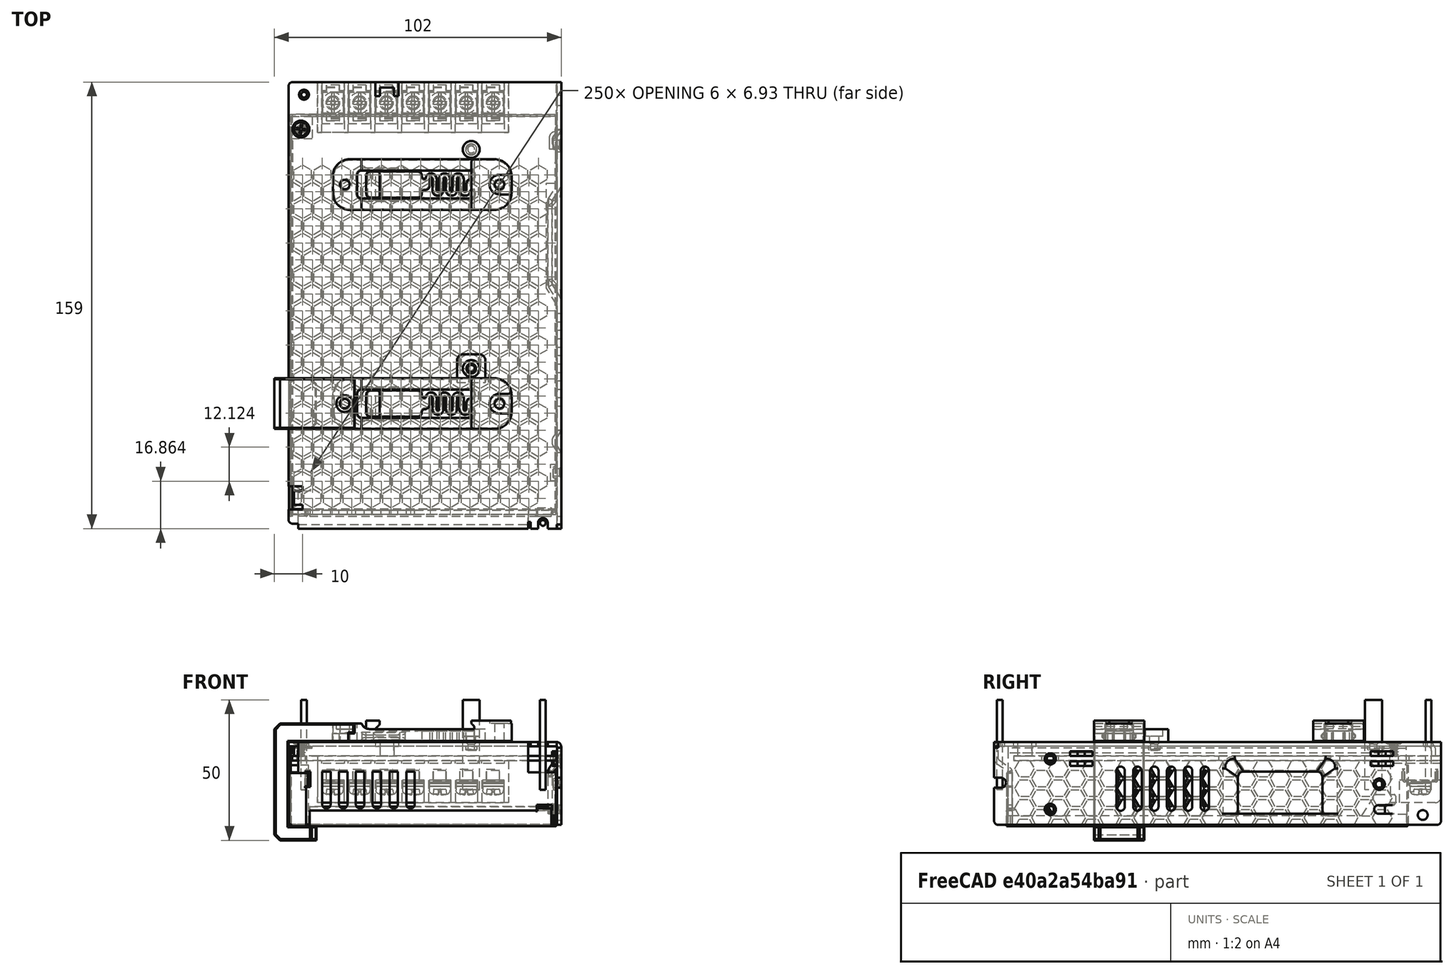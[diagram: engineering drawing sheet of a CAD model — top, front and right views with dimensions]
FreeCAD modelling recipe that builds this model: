
FCSTD DOCUMENT  (FreeCAD 0.18R16146 (Git))
Label: PSU-LRS-150-din-mount
License: Other
LicenseURL: GPL3
objects: Part::Cylinder×8, Part::Cut×7, Part::Feature×6, Part::Box×6, Part::Chamfer×4, Part::Fillet×2, Part::MultiFuse×2
note: 35 computed .brp shape members not serialized (recipe doc carries the construction recipe); baked Part::Feature solids carry a one-line shape summary decoded from their .brp

FEATURE [Part::Feature] Fusion006002011004053036004001028003005003  label="PSU-LRS-150-24"
  Placement = pos=(-16.5,22.5,17) rot=(-1,0,0;1.5708rad)
  shape: bbox 97.2 x 159 x 30.02 mm, 3511 faces (baked)
FEATURE [Part::Cylinder] Cylinder
  Angle = 360
  AttacherType = Attacher::AttachEngine3D
  Height = 32
  Placement = pos=(25.5,-55,0) rot=(0,0,1;1.5708rad)
  Radius = 1
FEATURE [Part::Cylinder] Cylinder001
  Angle = 360
  AttacherType = Attacher::AttachEngine3D
  Height = 32
  Placement = pos=(1.73e-14,78,0) rot=(0,0,1;1.5708rad)
  Radius = 3
FEATURE [Part::Cylinder] Cylinder002
  Angle = 360
  AttacherType = Attacher::AttachEngine3D
  Height = 32
  Placement = pos=(-59.5,97.5,0) rot=(0,0,1;1.5708rad)
  Radius = 1
FEATURE [Part::Cylinder] Cylinder003
  Angle = 360
  AttacherType = Attacher::AttachEngine3D
  Height = 5
  Placement = pos=(0,0,19) rot=(0,0,1;1.5708rad)
  Radius = 3
FEATURE [Part::Feature] Part__Feature822  label="RS-25 PSU Bracket"
  Placement = pos=(-17.4469,68.857,29.1031) rot=(0,1,0;3.14159rad)
  shape: bbox 63.6 x 18 x 7.6 mm, 163 faces (baked)
FEATURE [Part::Feature] Part__Feature823  label="RS-25 PSU Bracket001"
  Placement = pos=(-17.4469,-9.14304,29.1031) rot=(0,1,0;3.14159rad)
  shape: bbox 63.6 x 18 x 7.6 mm, 163 faces (baked)
FEATURE [Part::Box] Box  label="Cube"
  AttacherType = Attacher::AttachEngine3D
  Height = 4.6
  Length = 10
  Placement = pos=(-5,-5,17) rot=(0,0,1;0rad)
  Width = 10
FEATURE [Part::Fillet] Fillet
  Base = -> Box
  Edges = 2 edges r=2: [Edge3,Edge7]
FEATURE [Part::Box] Box001  label="Cube001"
  AttacherType = Attacher::AttachEngine3D
  Height = 4.6
  Length = 12
  Placement = pos=(-53.5,-24,20) rot=(0,0,1;0rad)
  Width = 22
FEATURE [Part::MultiFuse] Fusion
  Shapes = -> [Part__Feature823,Fillet]
FEATURE [Part::Cylinder] Cylinder004
  Angle = 360
  AttacherType = Attacher::AttachEngine3D
  Height = 32
  Placement = pos=(0,0,0) rot=(0,0,1;1.5708rad)
  Radius = 1.65
FEATURE [Part::Cut] Cut
  Base = -> Fusion
  Tool = -> Cylinder004
FEATURE [Part::Cut] Cut001
  Base = -> Cut
  Tool = -> Cylinder003
FEATURE [Part::Cylinder] Cylinder005
  Angle = 360
  AttacherType = Attacher::AttachEngine3D
  Height = 32
  Placement = pos=(-45,-12.5,21.6) rot=(0,0,1;1.5708rad)
  Radius = 3
FEATURE [Part::Cut] Cut002
  Base = -> Cut001
  Tool = -> Box001
FEATURE [Part::Cylinder] Cylinder006
  Angle = 360
  AttacherType = Attacher::AttachEngine3D
  Height = 32
  Placement = pos=(-45,-12.5,0) rot=(0,0,1;1.5708rad)
  Radius = 1.9
FEATURE [Part::Cut] Cut003  label="LRS-din-mount"
  Base = -> Cut002
  Tool = -> Cylinder006
FEATURE [Part::Box] Box003  label="Cube003"
  AttacherType = Attacher::AttachEngine3D
  Height = 5
  Length = 15
  Placement = pos=(-70,-21.5,-18) rot=(0,0,1;0rad)
  Width = 18
FEATURE [Part::Box] Box004  label="Cube004"
  AttacherType = Attacher::AttachEngine3D
  Height = 3
  Length = 11.4
  Placement = pos=(-49.3,-21.5,17) rot=(0,0,1;0rad)
  Width = 18
FEATURE [Part::Box] Box005  label="Cube005"
  AttacherType = Attacher::AttachEngine3D
  Height = 6.6
  Length = 28.4
  Placement = pos=(-70,-21.5,17) rot=(0,0,1;0rad)
  Width = 18
FEATURE [Part::Fillet] Fillet001
  Base = -> Box004
  Edges = 2 edges r=6: [Edge1,Edge3]
FEATURE [Part::Cut] Cut004
  Base = -> Box005
  Tool = -> Fillet001
FEATURE [Part::Cylinder] Cylinder007
  Angle = 360
  AttacherType = Attacher::AttachEngine3D
  Height = 32
  Placement = pos=(-45,-12.5,0) rot=(0,0,1;1.5708rad)
  Radius = 1.65
FEATURE [Part::Cut] Cut005
  Base = -> Cut004
  Tool = -> Cylinder007
FEATURE [Part::Cut] Cut006
  Base = -> Cut005
  Tool = -> Cylinder005
FEATURE [Part::Chamfer] Chamfer
  Base = -> Cut006
  Edges = 1 edges r=2: [Edge2]
FEATURE [Part::Box] Box002  label="Cube002"
  AttacherType = Attacher::AttachEngine3D
  Height = 31.6
  Length = 5
  Placement = pos=(-70,-21.5,-14) rot=(0,0,1;0rad)
  Width = 18
FEATURE [Part::Chamfer] Chamfer001
  Base = -> Box003
  Edges = 1 edges r=2: [Edge4]
FEATURE [Part::Chamfer] Chamfer002
  Base = -> Chamfer001
  Edges = 2 edges r=2: [Edge7,Edge14]
FEATURE [Part::MultiFuse] Fusion006002011004053036004001028003005004
  Shapes = -> [Chamfer,Box002,Chamfer002]
FEATURE [Part::Feature] Fusion006002011004053036004001028003005004001  label="Fusion006002011004053036004001028003005005"
  shape: bbox 28.4 x 18 x 41.6 mm, 21 faces (baked)
FEATURE [Part::Chamfer] Chamfer003  label="LRS-din-arm"
  Base = -> Fusion006002011004053036004001028003005004001
  Edges = 32 edges r=0.4: [Edge1,Edge4,Edge5,Edge7,Edge9,Edge12,Edge13,Edge14,Edge15,Edge16,Edge17,Edge18,Edge19,Edge20,Edge21,Edge22,Edge23,Edge24,Edge26,Edge28,Edge29,Edge30,Edge31,Edge35,Edge37,Edge41,Edge43,Edge44,Edge47,Edge48,Edge53,Edge54]
FEATURE [Part::Feature] Cut003001  label="LRS-din-mount001"
  shape: bbox 63.6 x 26.5 x 7.603 mm, 177 faces (baked)
FEATURE [Part::Feature] Chamfer003001  label="LRS-din-arm001"
  shape: bbox 28.4 x 18 x 41.6 mm, 61 faces (baked)
